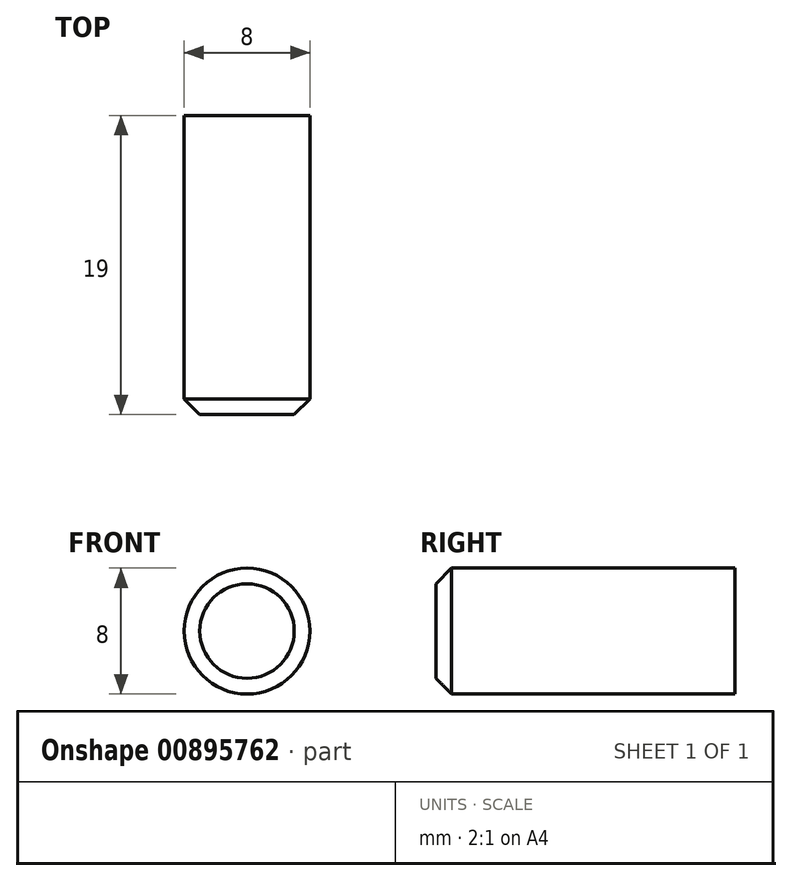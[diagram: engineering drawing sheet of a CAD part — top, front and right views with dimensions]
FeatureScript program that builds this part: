
annotation { "Feature Type Name" : "Feature", "Feature Type Description" : "" }
export const myFeature = defineFeature(function(context is Context, id is Id, definition is map)
    precondition{}
    {
        {
            var Q0;
            Q0=qCreatedBy(makeId("Front.planeOp"),FACE);
            var sketch = newSketch(context, id + "F0", { "sketchPlane" : qUnion([Q0])});
            skCircle(sketch, "E0", {"center": v(0, 0) * mm, "radius": 4 * mm});
            skSolve(sketch);
        }
        {
            var Q0;
            Q0=makeQuery(id+"F0.imprint","IMPRINT",FACE,{"disambiguationData":[TD([[makeQuery(id+"F0.imprint","IMPRINT",EDGE,{"derivedFrom":sQuery(id+"F0.wireOp",EDGE,"E0")}),1.0]])]});
            extrude(context, id + "F1", {"entities" : qUnion([Q0]), "offsetDistance" : 25 * mm, "depth" : 19 * mm});
        }
        {
            var Q0;
            Q0=makeQuery(id+"F1.opExtrude","CAP_EDGE",EDGE,{"disambiguationData":[OSD([sQuery(id+"F0.wireOp",EDGE,"E0")])],"isStart":false});
            chamfer(context, id + "F2", {"entities" : qUnion([Q0]), "width" : 1 * mm, "tangentPropagation" : true});
        }
    });
